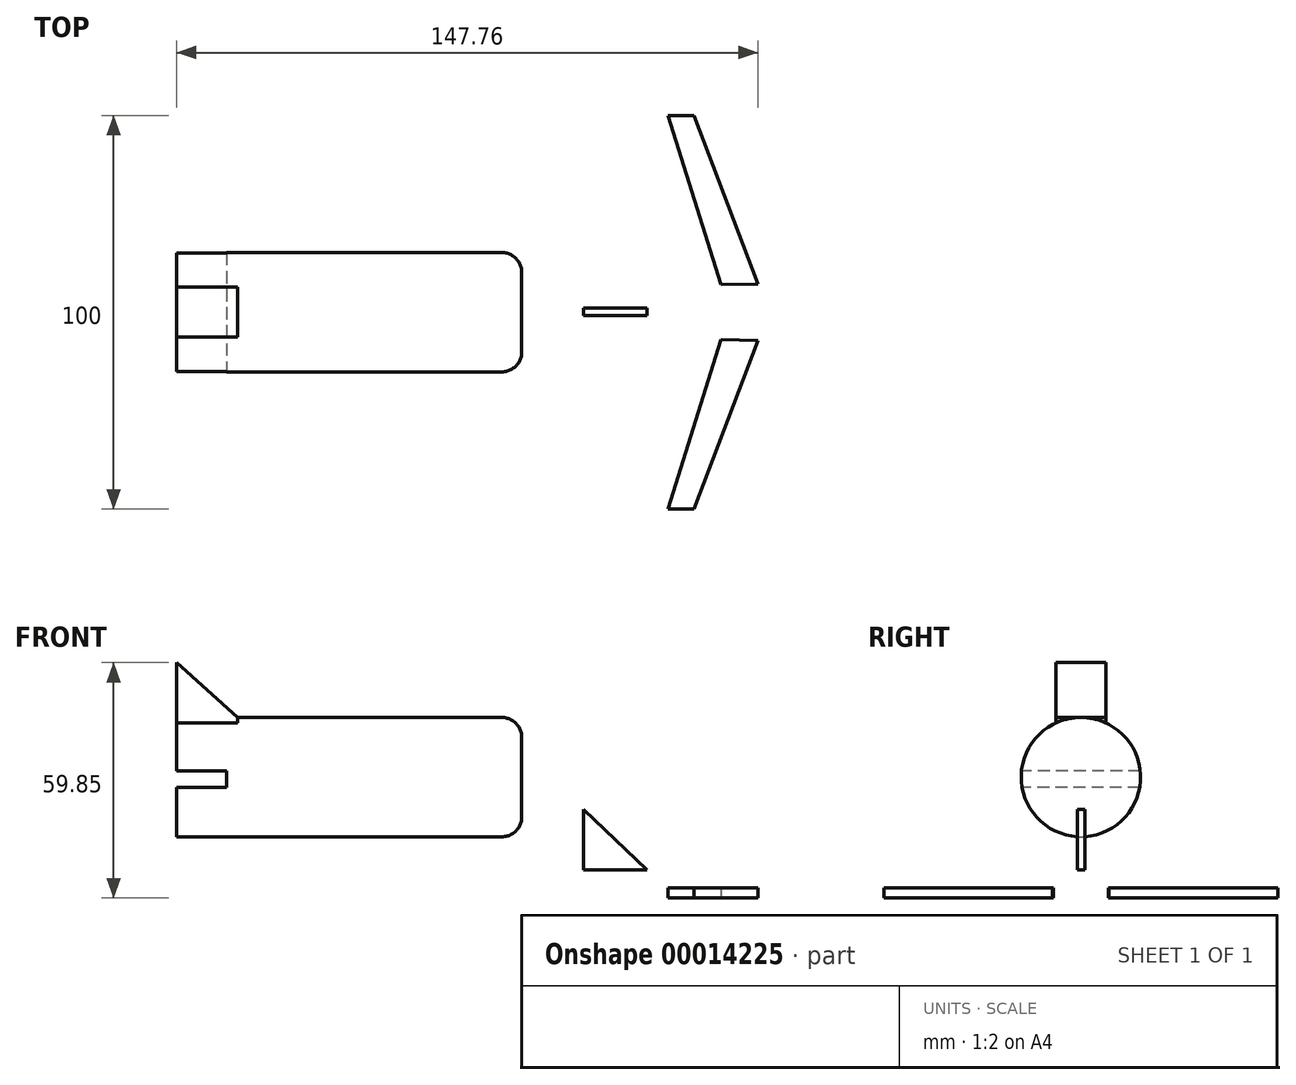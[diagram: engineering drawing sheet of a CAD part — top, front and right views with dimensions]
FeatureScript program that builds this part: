
annotation { "Feature Type Name" : "Feature", "Feature Type Description" : "" }
export const myFeature = defineFeature(function(context is Context, id is Id, definition is map)
    precondition{}
    {
        {
            var Q0;
            Q0=qCreatedBy(makeId("Front.planeOp"),FACE);
            var sketch = newSketch(context, id + "F0", { "sketchPlane" : qUnion([Q0])});
            skLineSegment(sketch, "E0", {"start": v(0, 0) * mm, "end": v(80.3, 0) * mm});
            skLineSegment(sketch, "E1", {"start": v(80.3, 0) * mm, "end": v(80.3, 7.1) * mm});
            skLineSegment(sketch, "E2", {"start": v(80.3, 7.1) * mm, "end": v(0, 7.1) * mm});
            skLineSegment(sketch, "E3", {"start": v(0, 7.1) * mm, "end": v(0, 0) * mm});
            skSolve(sketch);
        }
        {
            var Q0;
            Q0=sQuery(id+"F0.wireOp",EDGE,"E3");
            var Q1;
            Q1=sQuery(id+"F0.wireOp",EDGE,"E1");
            var Q2;
            Q2=sQuery(id+"F0.wireOp",EDGE,"E2");
            var Q3;
            Q3=sQuery(id+"F0.wireOp",EDGE,"E0");
            revolve(context, id + "F1", {"bodyType" : ToolBodyType.SURFACE, "surfaceEntities" : qUnion([Q0, Q1, Q2]), "axis" : qUnion([Q3]), "revolveType" : RevolveType.FULL});
        }
        {
            var Q0;
            Q0=makeQuery(id+"F1.opRevolve","SWEPT_EDGE",EDGE,{"disambiguationData":[OSD([sQuery(id+"F0.wireOp",VERTEX,"E2.start")])]});
            fillet(context, id + "F2", {"entities" : qUnion([Q0]), "radius" : 5.08 * mm, "tangentPropagation" : true, "allowEdgeOverflow" : false});
        }
        {
            var Q0;
            Q0=qCreatedBy(makeId("Front.planeOp"),FACE);
            var sketch = newSketch(context, id + "F3", { "sketchPlane" : qUnion([Q0])});
            skLineSegment(sketch, "E4", {"start": v(0, 7.08) * mm, "end": v(0, 22.55) * mm});
            skLineSegment(sketch, "E5", {"start": v(0, 22.55) * mm, "end": v(16.13, 7.11) * mm});
            skLineSegment(sketch, "E6", {"start": v(16.13, 7.11) * mm, "end": v(0, 7.11) * mm});
            skSolve(sketch);
        }
        {
            var Q0;
            {var subQ1=sQuery(id+"F3.wireOp",EDGE,"E5");Q0=makeQuery(id+"F3.imprint","IMPRINT",FACE,{"disambiguationData":[TD([[makeQuery(id+"F3.imprint","IMPRINT",EDGE,{"derivedFrom":subQ1}),-1.0]])]});}
            extrude(context, id + "F4", {"entities" : qUnion([Q0]), "depth" : 0.88 * mm, "hasSecondDirection" : true, "secondDirectionOppositeDirection" : true, "secondDirectionDepth" : 1.03 * mm});
        }
        {
            var Q0;
            Q0=qCreatedBy(makeId("Top.planeOp"),FACE);
            var sketch = newSketch(context, id + "F5", { "sketchPlane" : qUnion([Q0])});
            skLineSegment(sketch, "E7", {"start": v(44.35, -7.18) * mm, "end": v(28.09, -50) * mm});
            skLineSegment(sketch, "E8", {"start": v(28.09, -50) * mm, "end": v(21.47, -50) * mm});
            skLineSegment(sketch, "E9", {"start": v(21.47, -50) * mm, "end": v(34.96, -6.98) * mm});
            skLineSegment(sketch, "E10", {"start": v(34.96, -6.98) * mm, "end": v(44.35, -7.18) * mm});
            skSolve(sketch);
        }
        {
            var Q0;
            Q0=makeQuery(id+"F5.imprint","IMPRINT",FACE,{"disambiguationData":[TD([[makeQuery(id+"F5.imprint","IMPRINT",EDGE,{"derivedFrom":sQuery(id+"F5.wireOp",EDGE,"E7")}),-1.0]])]});
            extrude(context, id + "F6", {"entities" : qUnion([Q0]), "depth" : 2.54 * mm});
        }
        {
            var Q0;
            Q0=makeQuery(id+"F6.opExtrude","SWEPT_BODY",BODY,{"disambiguationData":[OSD([sQuery(id+"F5.wireOp",EDGE,"E7"),sQuery(id+"F5.wireOp",EDGE,"E8"),sQuery(id+"F5.wireOp",EDGE,"E9"),sQuery(id+"F5.wireOp",EDGE,"E10")])]});
            var Q1;
            Q1=qCreatedBy(makeId("Front.planeOp"),FACE);
            mirror(context, id + "F7", {"entities" : qUnion([Q0]), "mirrorPlane" : qUnion([Q1])});
        }
        {
            var Q0;
            Q0=makeQuery(id+"F1.opRevolve","SWEPT_FACE",FACE,{"disambiguationData":[OSD([sQuery(id+"F0.wireOp",EDGE,"E3")])]});
            var sketch = newSketch(context, id + "F8", { "sketchPlane" : qUnion([Q0])});
            skLineSegment(sketch, "E11.bottom", {"start": v(-7.7, 0.5) * mm, "end": v(7.48, 0.5) * mm});
            skLineSegment(sketch, "E11.top", {"start": v(-7.7, -0.76) * mm, "end": v(7.48, -0.76) * mm});
            skLineSegment(sketch, "E11.left", {"start": v(-7.7, 0.5) * mm, "end": v(-7.7, -0.76) * mm});
            skLineSegment(sketch, "E11.right", {"start": v(7.48, 0.5) * mm, "end": v(7.48, -0.76) * mm});
            skSolve(sketch);
        }
        {
            var Q0;
            {var subQ0=makeQuery(id+"F1.opRevolve","SWEPT_EDGE",EDGE,{"disambiguationData":[OSD([sQuery(id+"F0.wireOp",VERTEX,"E2.end")])]});var subQ3=sQuery(id+"F8.wireOp",EDGE,"E11.bottom");var subQ6=makeQuery(id+"F8.imprint","INTERSECT",VERTEX,{"disambiguationData":[OD(0.0)],"derivedFrom":[subQ0,subQ3]});Q0=makeQuery(id+"F8.imprint","IMPRINT",FACE,{"disambiguationData":[TD([[makeQuery(id+"F8.imprint","IMPRINT",EDGE,{"disambiguationData":[TD([[subQ6,-1.0]])],"derivedFrom":subQ3}),-1.0]])]});}
            extrude(context, id + "F9", {"entities" : qUnion([Q0]), "operationType" : NewBodyOperationType.REMOVE, "oppositeDirection" : true, "depth" : 15.22 * mm});
        }
        {
            var Q0;
            Q0=qCreatedBy(makeId("Front.planeOp"),FACE);
            var sketch = newSketch(context, id + "F10", { "sketchPlane" : qUnion([Q0])});
            skLineSegment(sketch, "E12", {"start": v(-103.41, 45.9) * mm, "end": v(-15.7, 45.9) * mm});
            skLineSegment(sketch, "E13", {"start": v(-103.41, 30.73) * mm, "end": v(-15.7, 30.73) * mm, "construction": true});
            skLineSegment(sketch, "E14", {"start": v(-103.41, 45.9) * mm, "end": v(-103.41, 30.73) * mm});
            skLineSegment(sketch, "E15", {"start": v(-15.7, 45.9) * mm, "end": v(-15.7, 30.73) * mm});
            skLineSegment(sketch, "E16", {"start": v(-103.41, 30.73) * mm, "end": v(-15.7, 30.73) * mm});
            skLineSegment(sketch, "E17", {"start": v(-103.41, 45.9) * mm, "end": v(-103.41, 59.85) * mm});
            skLineSegment(sketch, "E18", {"start": v(-103.41, 59.85) * mm, "end": v(-87.9, 45.9) * mm});
            skSolve(sketch);
        }
        {
            var Q0;
            Q0=makeQuery(id+"F10.imprint","IMPRINT",FACE,{"disambiguationData":[TD([[makeQuery(id+"F10.imprint","IMPRINT",EDGE,{"derivedFrom":sQuery(id+"F10.wireOp",EDGE,"E12")}),-1.0]])]});
            var Q1;
            Q1=sQuery(id+"F10.wireOp",EDGE,"E16");
            revolve(context, id + "F11", {"entities" : qUnion([Q0]), "axis" : qUnion([Q1]), "revolveType" : RevolveType.FULL});
        }
        {
            var Q0;
            Q0=makeQuery(id+"F11.opRevolve","SWEPT_FACE",FACE,{"disambiguationData":[OSD([sQuery(id+"F10.wireOp",EDGE,"E14")])]});
            var sketch = newSketch(context, id + "F12", { "sketchPlane" : qUnion([Q0])});
            skLineSegment(sketch, "E19.bottom", {"start": v(-17.77, 32.3) * mm, "end": v(16.96, 32.3) * mm});
            skLineSegment(sketch, "E19.top", {"start": v(-17.77, 28.16) * mm, "end": v(16.96, 28.16) * mm});
            skLineSegment(sketch, "E19.left", {"start": v(-17.77, 32.3) * mm, "end": v(-17.77, 28.16) * mm});
            skLineSegment(sketch, "E19.right", {"start": v(16.96, 32.3) * mm, "end": v(16.96, 28.16) * mm});
            skSolve(sketch);
        }
        {
            var Q0;
            {var subQ0=makeQuery(id+"F11.opRevolve","SWEPT_EDGE",EDGE,{"disambiguationData":[OSD([sQuery(id+"F10.wireOp",EDGE,"E12"),sQuery(id+"F10.wireOp",EDGE,"E14")])]});var subQ3=sQuery(id+"F12.wireOp",EDGE,"E19.bottom");var subQ6=makeQuery(id+"F12.imprint","INTERSECT",VERTEX,{"disambiguationData":[OD(0.0)],"derivedFrom":[subQ0,subQ3]});Q0=makeQuery(id+"F12.imprint","IMPRINT",FACE,{"disambiguationData":[TD([[makeQuery(id+"F12.imprint","IMPRINT",EDGE,{"disambiguationData":[TD([[subQ6,-1.0]])],"derivedFrom":subQ3}),-1.0]])]});}
            extrude(context, id + "F13", {"entities" : qUnion([Q0]), "operationType" : NewBodyOperationType.REMOVE, "oppositeDirection" : true, "depth" : 12.7 * mm});
        }
        {
            var Q0;
            {var subQ1=sQuery(id+"F10.wireOp",EDGE,"E17");Q0=makeQuery(id+"F10.imprint","IMPRINT",FACE,{"disambiguationData":[TD([[makeQuery(id+"F10.imprint","IMPRINT",EDGE,{"derivedFrom":subQ1}),-1.0]])]});}
            extrude(context, id + "F14", {"entities" : qUnion([Q0]), "endBound" : BoundingType.SYMMETRIC, "depth" : 12.7 * mm});
        }
        {
            var Q0;
            Q0=makeQuery(id+"F14.opExtrude","SWEPT_FACE",FACE,{"disambiguationData":[OSD([sQuery(id+"F10.wireOp",EDGE,"E12")])]});
            extrude(context, id + "F15", {"entities" : qUnion([Q0]), "operationType" : NewBodyOperationType.ADD, "depth" : 2.54 * mm});
        }
        {
            var Q0;
            Q0=makeQuery(id+"F11.opRevolve","SWEPT_EDGE",EDGE,{"disambiguationData":[OSD([sQuery(id+"F10.wireOp",EDGE,"E12"),sQuery(id+"F10.wireOp",EDGE,"E15")])]});
            fillet(context, id + "F16", {"entities" : qUnion([Q0]), "radius" : 5.08 * mm, "tangentPropagation" : true, "allowEdgeOverflow" : false});
        }
    });
